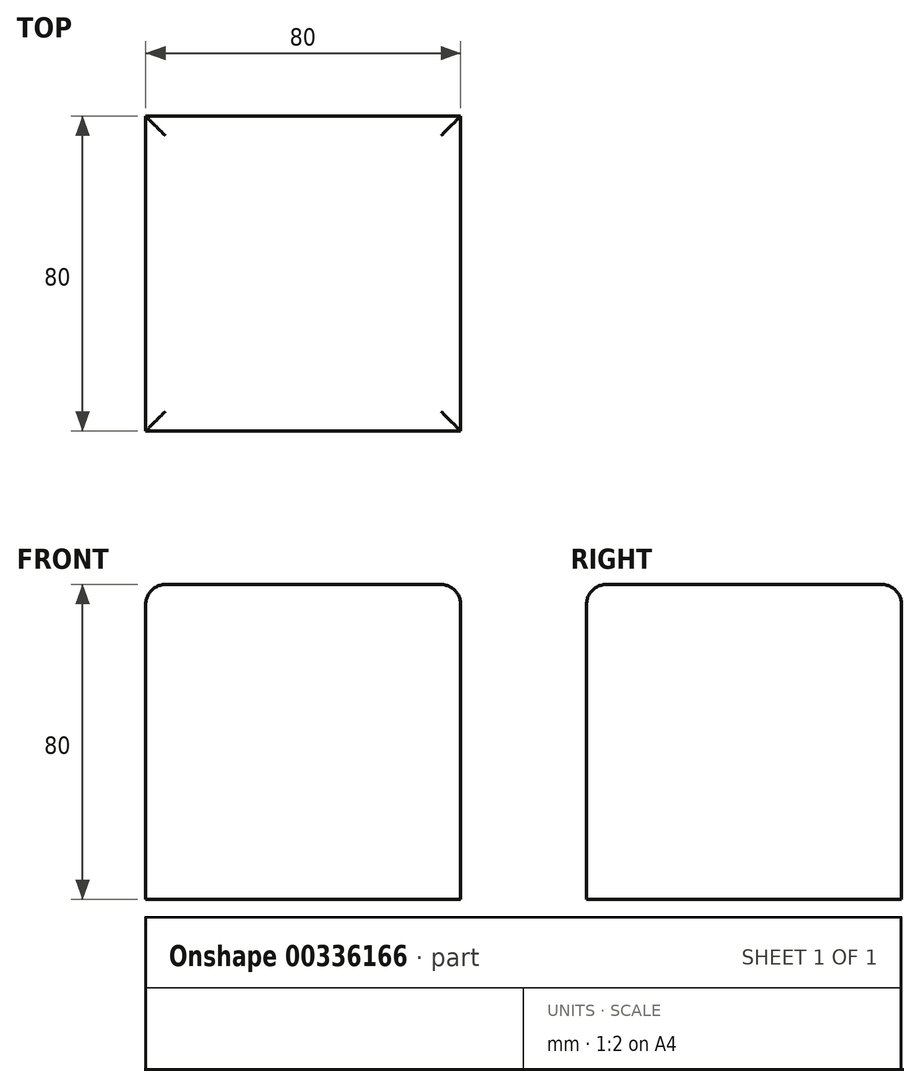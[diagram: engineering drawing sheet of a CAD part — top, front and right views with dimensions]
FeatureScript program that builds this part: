
annotation { "Feature Type Name" : "Feature", "Feature Type Description" : "" }
export const myFeature = defineFeature(function(context is Context, id is Id, definition is map)
    precondition{}
    {
        {
            var Q0;
            Q0=qCreatedBy(makeId("Top.planeOp"),FACE);
            var sketch = newSketch(context, id + "F0", { "sketchPlane" : qUnion([Q0])});
            skLineSegment(sketch, "E0.bottom", {"start": v(-40, -40) * mm, "end": v(40, -40) * mm});
            skLineSegment(sketch, "E0.top", {"start": v(-40, 40) * mm, "end": v(40, 40) * mm});
            skLineSegment(sketch, "E0.left", {"start": v(-40, -40) * mm, "end": v(-40, 40) * mm});
            skLineSegment(sketch, "E0.right", {"start": v(40, -40) * mm, "end": v(40, 40) * mm});
            skPoint(sketch, "E0.middle", {"position": v(0, 0) * mm});
            skSolve(sketch);
        }
        {
            var Q0;
            Q0=makeQuery(id+"F0.imprint","IMPRINT",FACE,{"disambiguationData":[TD([[makeQuery(id+"F0.imprint","IMPRINT",EDGE,{"derivedFrom":sQuery(id+"F0.wireOp",EDGE,"E0.bottom")}),1.0]])]});
            extrude(context, id + "F1", {"entities" : qUnion([Q0]), "endBound" : BoundingType.SYMMETRIC, "depth" : 80 * mm});
        }
        {
            var Q0;
            Q0=makeQuery(id+"F1.opExtrude","CAP_EDGE",EDGE,{"disambiguationData":[OSD([sQuery(id+"F0.wireOp",EDGE,"E0.left")])],"isStart":false});
            var Q1;
            Q1=makeQuery(id+"F1.opExtrude","CAP_FACE",FACE,{"disambiguationData":[OSD([sQuery(id+"F0.wireOp",EDGE,"E0.bottom"),sQuery(id+"F0.wireOp",EDGE,"E0.top"),sQuery(id+"F0.wireOp",EDGE,"E0.left"),sQuery(id+"F0.wireOp",EDGE,"E0.right")])],"isStart":false});
            fillet(context, id + "F2", {"entities" : qUnion([Q0, Q1]), "radius" : 5 * mm, "tangentPropagation" : true, "allowEdgeOverflow" : false});
        }
    });
